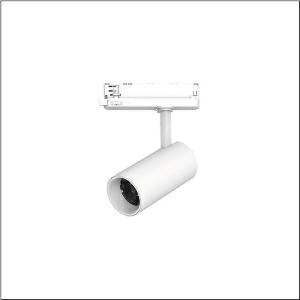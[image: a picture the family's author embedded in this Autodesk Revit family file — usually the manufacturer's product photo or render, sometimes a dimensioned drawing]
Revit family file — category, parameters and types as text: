
# Revit family: spot_31_slim_51sf127fa1b
name_source: partatom
category: Lighting Fixtures
units: mm (PartAtom-declared; Revit-internal decimal feet)

## family parameters
Cut with Voids When Loaded = No
Host = Face
Light Source = No
Part Type = Normal
Room Calculation Point = No
Round Connector Dimension = Use Diameter
Shared = No

## types (1)
- Spot 31 Slim (1 x LED, 2090 lm, 16.3 W, 2700K)
    Apparent Load = 16 VA
    CIE Flux Codes = 94 98 99 100 100
    Color Rendering = 90
    Color Temperature = 2700K
    Default Elevation = 1800 mm
    Description = Spot 31 Slim, directional spotlight, light control with reflector, of aluminium, LED rated luminous flux: 2.100lm, light colour: 927, control gear: ECG, with 3-phase adapter, mains connection: 220..240V, AC, 50/60Hz, housing, of aluminium, traffic white (RAL 9016), diameter: 70mm, adapter, of plastic, protection rating (complete): IP20, insulation class (complete): insulation class I (protective earthing), certification: CE, impact resistance: IK02, packaging unit: 1 piece
    Height = 210 mm
    Lamp = 1 x LED
    Lamp Light Flux = 2090 lm
    Lamp Power = 16.3 W
    Lamp count = 1
    Length = 70 mm
    Luminous efficacy = 128 lm/W
    Manufacturer = Siteco
    ModVariant = No
    Model = 51SF127FA1B
    Mounting Place = Ceiling
    Mounting Type = Pendant
    Number of Poles = 1
    OnlyDefault = Yes
    Power Factor = 1
    Product Name = Spot 31 Slim
    Product group = directional spotlight
    ProductGroupID = 905
    Protection Class = Protection class I
    Protection Degree = IP 20
    RLX_Detail_Level = 1
    RLX_Emergency_Light_Flux = 0 lm
    RLX_Emergency_Type = 0
    RLX_Emergency_Type_DB = No
    RlxData = <blob elided: 13505 chars, md5=d600500d>
    Socket = socket
    Standby Power = 0 W
    System Light Flux = 2090 lm
    System Power = 16 W
    Type Comments = Product without accessories
    Type Image = l_1228470.jpg
    URL = http://relux.com
    VarID = ---
    Voltage = 0 V
    Weight = 0.00 kg
    Width = 0 mm  [stored 0 ft]

note: [stored X ft] marks values corroborated as IEEE doubles in the binary element streams (Revit-internal decimal feet)

## geometry (parser evidence)
native form markers: Sweep x12
no freeform markers — native parametric forms only
